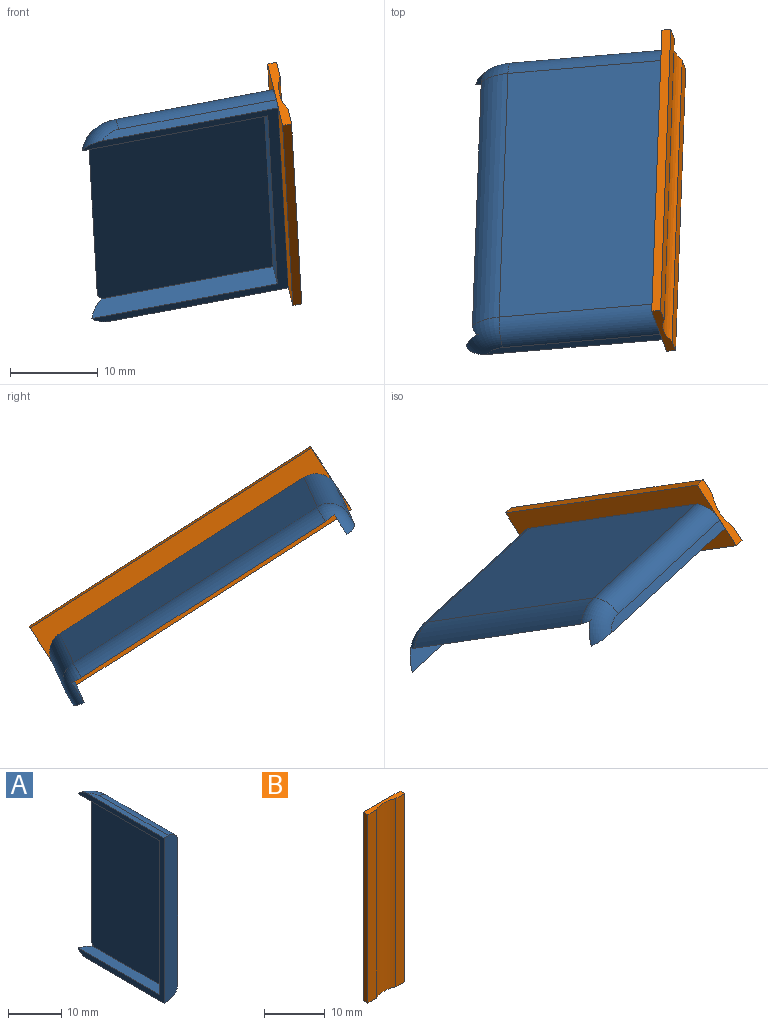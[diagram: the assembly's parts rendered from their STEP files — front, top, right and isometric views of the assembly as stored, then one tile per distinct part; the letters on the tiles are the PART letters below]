
ASSEMBLY  parts=2 mates=1
PART A: 14 faces, bbox 5.3x23.6x38.1 mm
  f0: plane 38.1x22.86mm, normal (-1,0,0), area 101.5mm2, adj f1,f3,f4,f5,f7,f8,f11,f13
  f1: plane 38.1x3.67mm, normal (0,-1,0), area 137.1mm2, adj f0,f2,f3,f4,f10,f12
  f2: plane 33.02x18.34mm, normal (1,0,0), area 605.5mm2, adj f1,f9,f10,f12
  f3: plane 20.45x1.13mm, normal (0,0,1), area 22.4mm2, adj f0,f1,f12,f13
  f4: plane 20.45x1.13mm, normal (0,0,-1), area 22.4mm2, adj f0,f1,f10,f11
  f5: plane 35.56x2.4mm, normal (0,1,0), area 85.4mm2, adj f0,f6,f7,f8
  f6: plane 35.56x20.43mm, normal (-1,0,0), area 725.9mm2, adj f5,f7,f8,f9,f11,f13
  f7: plane 21.59x2.4mm, normal (0,0,-1), area 50.3mm2, adj f0,f5,f6,f13
  f8: plane 21.59x2.4mm, normal (0,0,1), area 50.3mm2, adj f0,f5,f6,f11
  f9: cylinder r=5.08mm len=33.02mm, axis (0,0,-1), area 121.2mm2, adj f2,f6,f11,f13
  f10: cylinder r=2.54mm len=18.34mm, axis (0,1,0), area 73.2mm2, adj f1,f2,f4,f11
  f11: torus R=2.54mm, axis (0,0,1), area 16.4mm2, adj f0,f4,f6,f8,f9,f10
  f12: cylinder r=2.54mm len=18.34mm, axis (0,-1,0), area 73.2mm2, adj f1,f2,f3,f13
  f13: torus R=2.54mm, axis (0,0,1), area 16.4mm2, adj f0,f3,f6,f7,f9,f12
PART B: 8 faces, bbox 8.5x1x38.1 mm
  f0: plane 38.1x2mm, normal (0,-1,0), area 76.3mm2, adj f1,f5,f6,f7
  f1: plane 38.1x1.03mm, normal (1,0,0), area 39.3mm2, adj f0,f2,f6,f7
  f2: plane 38.1x8.54mm, normal (0,1,0), area 325.5mm2, adj f1,f3,f6,f7
  f3: plane 38.1x1.03mm, normal (-1,0,0), area 39.3mm2, adj f2,f4,f6,f7
  f4: plane 38.1x2mm, normal (0,-1,0), area 76.3mm2, adj f3,f5,f6,f7
  f5: cylinder r=5.24mm len=38.1mm, axis (0,0,1), area 178.8mm2, adj f0,f4,f6,f7
  f6: plane 8.54x1.03mm, normal (0,0,-1), area 7.2mm2, adj f0,f1,f2,f3,f4,f5
  f7: plane 8.54x1.03mm, normal (0,0,1), area 7.2mm2, adj f0,f1,f2,f3,f4,f5
PLACE A rot(axis=(0.35,-0.46,0.81),111.8deg) t=(73.82,72.29,-53.98)mm
PLACE B rot(axis=(0.35,-0.46,0.81),111.8deg) t=(45.26,94.88,-20.27)mm
MATE fastened B.f2 <-> A.f1  axis (-0.98,-0.08,-0.18) through (39.04,78.36,-11.07)mm
